# Revit family: KB310-SSRE-OPEN-01
name_source: partatom
category: Equipement spécialisé
units: mm (PartAtom-declared; Revit-internal decimal feet)

## family parameters
Autoriser la découpe dans les vues = Non
Conserver l'orientation des annotations = Non
Cote de connecteur circulaire = Utiliser le diamètre
Couper avec des vides une fois chargée = Non
Hôte = Face
Numéro OmniClass = 23.40.20.21
Partagée = Oui
Repère de localisation dans la pièce = Non
Titre OmniClass = Toilet and Bath Specialties
Type d'élément = Normal

## types (1)
- KB310-SSRE_Open Position
    ADA Compliant = Oui
    Code d'assemblage = E2010
    Commentaires du type = Available Colors: Grey with Stainless Steel
    Description = KB310-SSRE Baby Changing Station Open Position
    Elévation par défaut = 23 1/8"
    Fabricant = Koala Kare
    Height = 26 7/32"
    Installation Type = Recessed in Wall
    Length = 17 13/32"
    Material = High Density Polyethylene- Koala Kare-Grey
    Modèle = KB310-SSRE
    Nom du vendeur / Seller's name = ANOX Diffusion
    Omniclass Table 23 Code = 23.40.20.21
    Omniclass Table 23 Title = Toilet and Bath Specialties
    Price = Prices may vary. Please consult Manufacturer Representative for most up-to-date price list.
    URL = https://www.anox.fr
    Warranty Information = 5 Year Limited Warranty
    Width = 41 5/16"

## geometry (parser evidence)
native form markers: Sweep x2
no freeform markers — native parametric forms only
